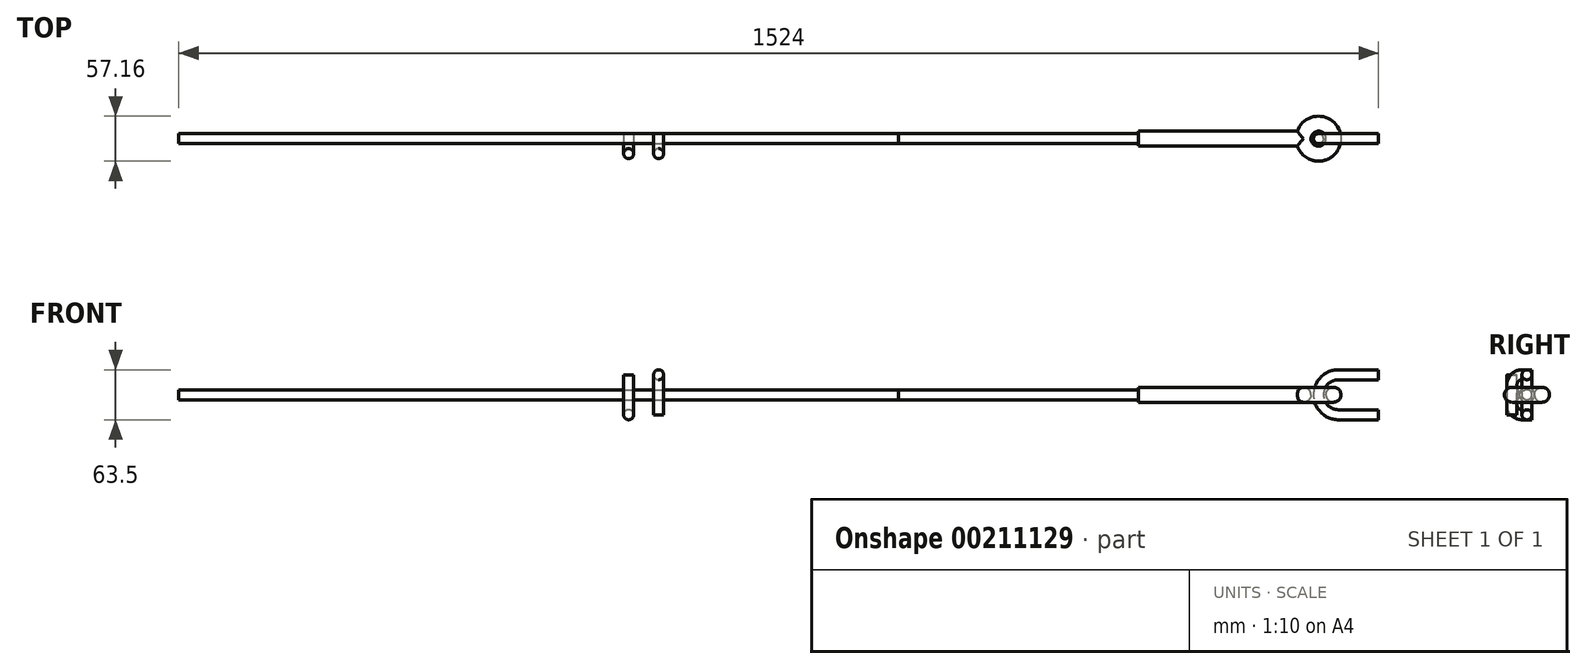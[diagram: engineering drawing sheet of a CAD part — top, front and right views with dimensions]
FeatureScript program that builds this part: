
annotation { "Feature Type Name" : "Feature", "Feature Type Description" : "" }
export const myFeature = defineFeature(function(context is Context, id is Id, definition is map)
    precondition{}
    {
        {
            var Q0;
            Q0=qCreatedBy(makeId("Right.planeOp"),FACE);
            var sketch = newSketch(context, id + "F0", { "sketchPlane" : qUnion([Q0])});
            skLineSegment(sketch, "E0", {"start": v(0, 25.4) * mm, "end": v(0, 0) * mm, "construction": true});
            skCircle(sketch, "E1", {"center": v(-6.35, 25.4) * mm, "radius": 6.35 * mm});
            skLineSegment(sketch, "E2", {"start": v(0, 0) * mm, "end": v(0, -25.4) * mm, "construction": true});
            skCircle(sketch, "E3", {"center": v(-6.35, -25.4) * mm, "radius": 6.35 * mm, "construction": true});
            skSolve(sketch);
        }
        {
            var Q0;
            Q0=qCreatedBy(makeId("Front.planeOp"),FACE);
            var sketch = newSketch(context, id + "F1", { "sketchPlane" : qUnion([Q0])});
            skPoint(sketch, "E4.0", {"position": v(0, 25.4) * mm});
            skPoint(sketch, "E4.1", {"position": v(0, -25.4) * mm});
            skLineSegment(sketch, "E5.bottom", {"start": v(0, 25.4) * mm, "end": v(-50.8, 25.4) * mm});
            skLineSegment(sketch, "E5.top", {"start": v(0, -25.4) * mm, "end": v(-50.8, -25.4) * mm});
            skLineSegment(sketch, "E5.left", {"start": v(0, 25.4) * mm, "end": v(0, -25.4) * mm, "construction": true});
            skLineSegment(sketch, "E5.right", {"start": v(-76.2, 0) * mm, "end": v(-76.2, 0) * mm});
            skPoint(sketch, "E6.visualSharp", {"position": v(-76.2, 25.4) * mm});
            skArc(sketch, "E6.filletArc", {"start": v(-50.8, 25.4) * mm, "mid": v(-68.76, 17.96) * mm, "end": v(-76.2, 0) * mm});
            skPoint(sketch, "E7.visualSharp", {"position": v(-76.2, -25.4) * mm});
            skArc(sketch, "E7.filletArc", {"start": v(-76.2, 0) * mm, "mid": v(-68.76, -17.96) * mm, "end": v(-50.8, -25.4) * mm});
            skSolve(sketch);
        }
        {
            var Q0;
            Q0 = qSketchRegion(id + "F0", true);
            var Q1;
            Q1 = qConstructionFilter(qBodyType(qCreatedBy(id + "F1" ,EDGE), BodyType.WIRE), ConstructionObject.NO);
            sweep(context, id + "F2", {"profiles" : qUnion([Q0]), "path" : qUnion([Q1])});
        }
        {
            var Q0;
            Q0=qCreatedBy(makeId("Top.planeOp"),FACE);
            var sketch = newSketch(context, id + "F3", { "sketchPlane" : qUnion([Q0])});
            skPoint(sketch, "E8.0", {"position": v(0, -6.35) * mm});
            skPoint(sketch, "E9", {"position": v(-152.4, -6.35) * mm});
            skLineSegment(sketch, "E10", {"start": v(-152.4, -6.35) * mm, "end": v(0, -6.35) * mm, "construction": true});
            skSolve(sketch);
        }
        {
            var Q0;
            Q0=sQuery(id+"F0.wireOp",VERTEX,"E1.center");
            var Q1;
            Q1=sQuery(id+"F0.wireOp",VERTEX,"E3.center");
            var Q2;
            Q2=sQuery(id+"F3.wireOp",VERTEX,"E9");
            cPlane(context, id + "F4", {"entities" : qUnion([Q0, Q1, Q2]), "cplaneType" : CPlaneType.THREE_POINT, "offset" : 25.4 * mm, "width" : 152.4 * mm, "height" : 152.4 * mm});
        }
        {
            var Q0;
            Q0=qCreatedBy(id+"F4.planeOp",FACE);
            var sketch = newSketch(context, id + "F5", { "sketchPlane" : qUnion([Q0])});
            skPoint(sketch, "E11.0", {"position": v(-50.8, 0) * mm});
            skLineSegment(sketch, "E11.1", {"start": v(-152.4, 0) * mm, "end": v(0, 0) * mm, "construction": true});
            skCircle(sketch, "E12", {"center": v(-95.25, 0) * mm, "radius": 9.53 * mm});
            skSolve(sketch);
        }
        {
            var Q0;
            Q0=qCreatedBy(makeId("Top.planeOp"),FACE);
            var sketch = newSketch(context, id + "F6", { "sketchPlane" : qUnion([Q0])});
            skPoint(sketch, "E13.2", {"position": v(-76.2, -6.35) * mm});
            skCircle(sketch, "E14", {"center": v(-76.2, -6.35) * mm, "radius": 15.88 * mm});
            skSolve(sketch);
        }
        {
            var Q0;
            Q0 = qSketchRegion(id + "F5", true);
            var Q1;
            Q1 = qConstructionFilter(qBodyType(qCreatedBy(id + "F6" ,EDGE), BodyType.WIRE), ConstructionObject.NO);
            sweep(context, id + "F7", {"profiles" : qUnion([Q0]), "path" : qUnion([Q1])});
        }
        {
            var Q0;
            Q0=qCreatedBy(makeId("Right.planeOp"),FACE);
            cPlane(context, id + "F8", {"entities" : qUnion([Q0]), "cplaneType" : CPlaneType.OFFSET, "offset" : 304.8 * mm, "oppositeDirection" : true, "width" : 152.4 * mm, "height" : 152.4 * mm});
        }
        {
            var Q0;
            Q0=qCreatedBy(id+"F8.planeOp",FACE);
            var sketch = newSketch(context, id + "F9", { "sketchPlane" : qUnion([Q0])});
            skPoint(sketch, "E15.0", {"position": v(-6.35, 0) * mm});
            skCircle(sketch, "E16", {"center": v(-6.35, 0) * mm, "radius": 9.53 * mm});
            skSolve(sketch);
        }
        {
            var Q0;
            Q0 = qSketchRegion(id + "F9", true);
            var Q1;
            Q1=makeQuery(id+"F7.opSweep","SWEPT_FACE",FACE,{"disambiguationData":[OSD([sQuery(id+"F5.wireOp",EDGE,"E12"),sQuery(id+"F6.wireOp",EDGE,"E14")])]});
            extrude(context, id + "F10", {"entities" : qUnion([Q0]), "operationType" : NewBodyOperationType.ADD, "endBound" : BoundingType.UP_TO_SURFACE, "endBoundEntityFace" : qUnion([Q1]), "depth" : 25.4 * mm});
        }
        {
            var Q0;
            Q0=makeQuery(id+"F10.opExtrude","CAP_FACE",FACE,{"disambiguationData":[OSD([sQuery(id+"F9.wireOp",EDGE,"E16")])],"isStart":true});
            var sketch = newSketch(context, id + "F11", { "sketchPlane" : qUnion([Q0])});
            skCircle(sketch, "E17.0", {"center": v(6.35, 0) * mm, "radius": 9.53 * mm, "construction": true});
            skCircle(sketch, "E18", {"center": v(6.35, 0) * mm, "radius": 6.35 * mm});
            skSolve(sketch);
        }
        {
            var Q0;
            Q0 = qSketchRegion(id + "F11", true);
            extrude(context, id + "F12", {"entities" : qUnion([Q0]), "depth" : 304.8 * mm});
        }
        {
            var Q0;
            Q0=makeQuery(id+"F12.opExtrude","CAP_FACE",FACE,{"disambiguationData":[OSD([sQuery(id+"F11.wireOp",EDGE,"E18")])],"isStart":false});
            var sketch = newSketch(context, id + "F13", { "sketchPlane" : qUnion([Q0])});
            skCircle(sketch, "E19.0", {"center": v(6.35, 0) * mm, "radius": 6.35 * mm});
            skSolve(sketch);
        }
        {
            var Q0;
            Q0 = qSketchRegion(id + "F13", true);
            extrude(context, id + "F14", {"entities" : qUnion([Q0]), "depth" : 914.4 * mm});
        }
        {
            var Q0;
            Q0=qCreatedBy(makeId("Front.planeOp"),FACE);
            var sketch = newSketch(context, id + "F15", { "sketchPlane" : qUnion([Q0])});
            skCircle(sketch, "E20", {"center": v(-914.4, 25.4) * mm, "radius": 6.35 * mm});
            skSolve(sketch);
        }
        {
            var Q0;
            Q0=qCreatedBy(makeId("Front.planeOp"),FACE);
            var sketch = newSketch(context, id + "F16", { "sketchPlane" : qUnion([Q0])});
            skCircle(sketch, "E21", {"center": v(-952.5, -25.4) * mm, "radius": 6.35 * mm});
            skPoint(sketch, "E22.0", {"position": v(-914.4, 25.4) * mm});
            skSolve(sketch);
        }
        {
            var Q0;
            Q0=qCreatedBy(id+"F8.planeOp",FACE);
            var sketch = newSketch(context, id + "F17", { "sketchPlane" : qUnion([Q0])});
            skPoint(sketch, "E23.0", {"position": v(0, 25.4) * mm});
            skLineSegment(sketch, "E24", {"start": v(0, 25.4) * mm, "end": v(-12.7, 25.4) * mm});
            skLineSegment(sketch, "E25", {"start": v(-25.4, 12.7) * mm, "end": v(-25.4, -25.4) * mm});
            skPoint(sketch, "E26.visualSharp", {"position": v(-25.4, 25.4) * mm});
            skArc(sketch, "E26.filletArc", {"start": v(-12.7, 25.4) * mm, "mid": v(-21.68, 21.68) * mm, "end": v(-25.4, 12.7) * mm});
            skSolve(sketch);
        }
        {
            var Q0;
            Q0=qCreatedBy(id+"F8.planeOp",FACE);
            var sketch = newSketch(context, id + "F18", { "sketchPlane" : qUnion([Q0])});
            skPoint(sketch, "E27.0", {"position": v(0, -25.4) * mm});
            skLineSegment(sketch, "E28", {"start": v(0, -25.4) * mm, "end": v(-12.7, -25.4) * mm});
            skLineSegment(sketch, "E29", {"start": v(-25.4, -12.7) * mm, "end": v(-25.4, 25.4) * mm});
            skPoint(sketch, "E30.0", {"position": v(-25.4, -25.4) * mm});
            skPoint(sketch, "E30.1", {"position": v(-25.4, 25.4) * mm});
            skArc(sketch, "E31.0", {"start": v(-12.7, 25.4) * mm, "mid": v(-21.68, 21.68) * mm, "end": v(-25.4, 12.7) * mm, "construction": true});
            skArc(sketch, "E32.filletArc", {"start": v(-25.4, -12.7) * mm, "mid": v(-21.68, -21.68) * mm, "end": v(-12.7, -25.4) * mm});
            skSolve(sketch);
        }
        {
            var Q0;
            Q0 = qSketchRegion(id + "F15", true);
            var Q1;
            Q1 = qConstructionFilter(qBodyType(qCreatedBy(id + "F17" ,EDGE), BodyType.WIRE), ConstructionObject.NO);
            sweep(context, id + "F19", {"profiles" : qUnion([Q0]), "path" : qUnion([Q1])});
        }
        {
            var Q0;
            Q0 = qSketchRegion(id + "F16", true);
            var Q1;
            Q1 = qConstructionFilter(qBodyType(qCreatedBy(id + "F18" ,EDGE), BodyType.WIRE), ConstructionObject.NO);
            sweep(context, id + "F20", {"profiles" : qUnion([Q0]), "path" : qUnion([Q1])});
        }
    });
